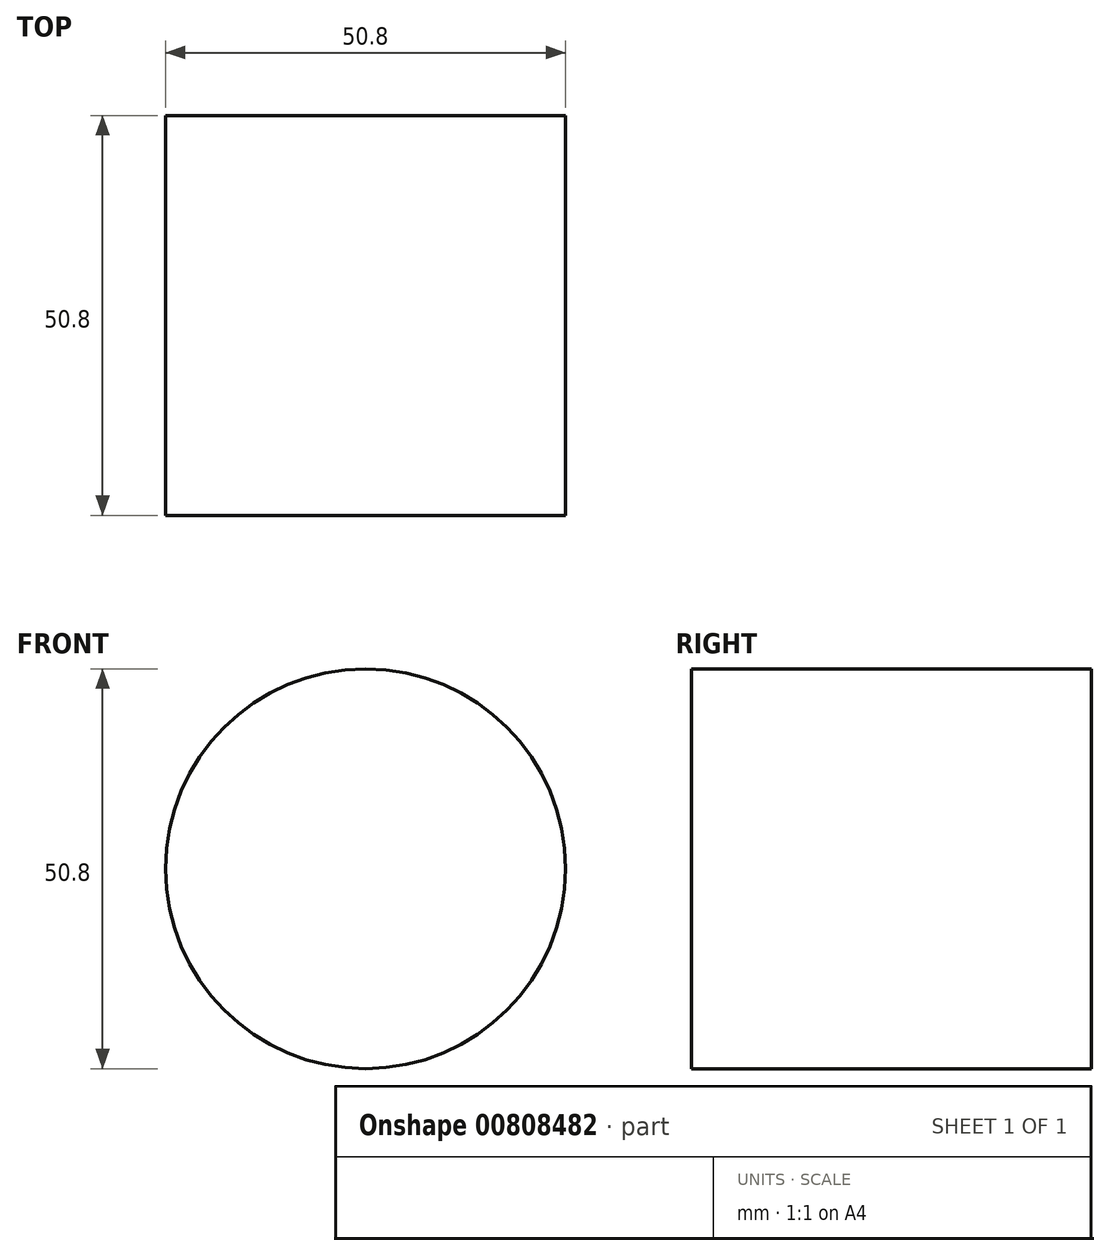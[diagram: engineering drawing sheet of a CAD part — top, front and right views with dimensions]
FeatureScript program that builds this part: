
annotation { "Feature Type Name" : "Feature", "Feature Type Description" : "" }
export const myFeature = defineFeature(function(context is Context, id is Id, definition is map)
    precondition{}
    {
        {
            var Q0;
            Q0=qCreatedBy(makeId("Front.planeOp"),FACE);
            var sketch = newSketch(context, id + "F0", { "sketchPlane" : qUnion([Q0])});
            skLineSegment(sketch, "E0", {"start": v(-61.19, 55.87) * mm, "end": v(-48.81, 55.87) * mm});
            skPoint(sketch, "E1.startSnap0", {"position": v(-36.43, 55.87) * mm});
            skPoint(sketch, "E1.endSnap0", {"position": v(-36.43, 55.87) * mm});
            skCircle(sketch, "E2", {"center": v(41.63, 27.23) * mm, "radius": 25.4 * mm});
            skPoint(sketch, "E3.newPointA", {"position": v(-11.67, 55.87) * mm});
            skArc(sketch, "E3.filletArc", {"start": v(-48.81, 55.87) * mm, "mid": v(-39.85, 59.57) * mm, "end": v(-36.11, 68.53) * mm});
            skPoint(sketch, "E1.start.orphan", {"position": v(-36.43, -32.35) * mm});
            skLineSegment(sketch, "E4", {"start": v(56.28, 6.48) * mm, "end": v(34.74, -8.72) * mm});
            skSolve(sketch);
        }
        {
            var Q0;
            Q0=sQuery(id+"F0.wireOp",EDGE,"E2");
            extrude(context, id + "F1", {"bodyType" : ToolBodyType.SURFACE, "surfaceEntities" : qUnion([Q0]), "depth" : 50.8 * mm, "offsetDistance" : 25.4 * mm});
        }
    });
